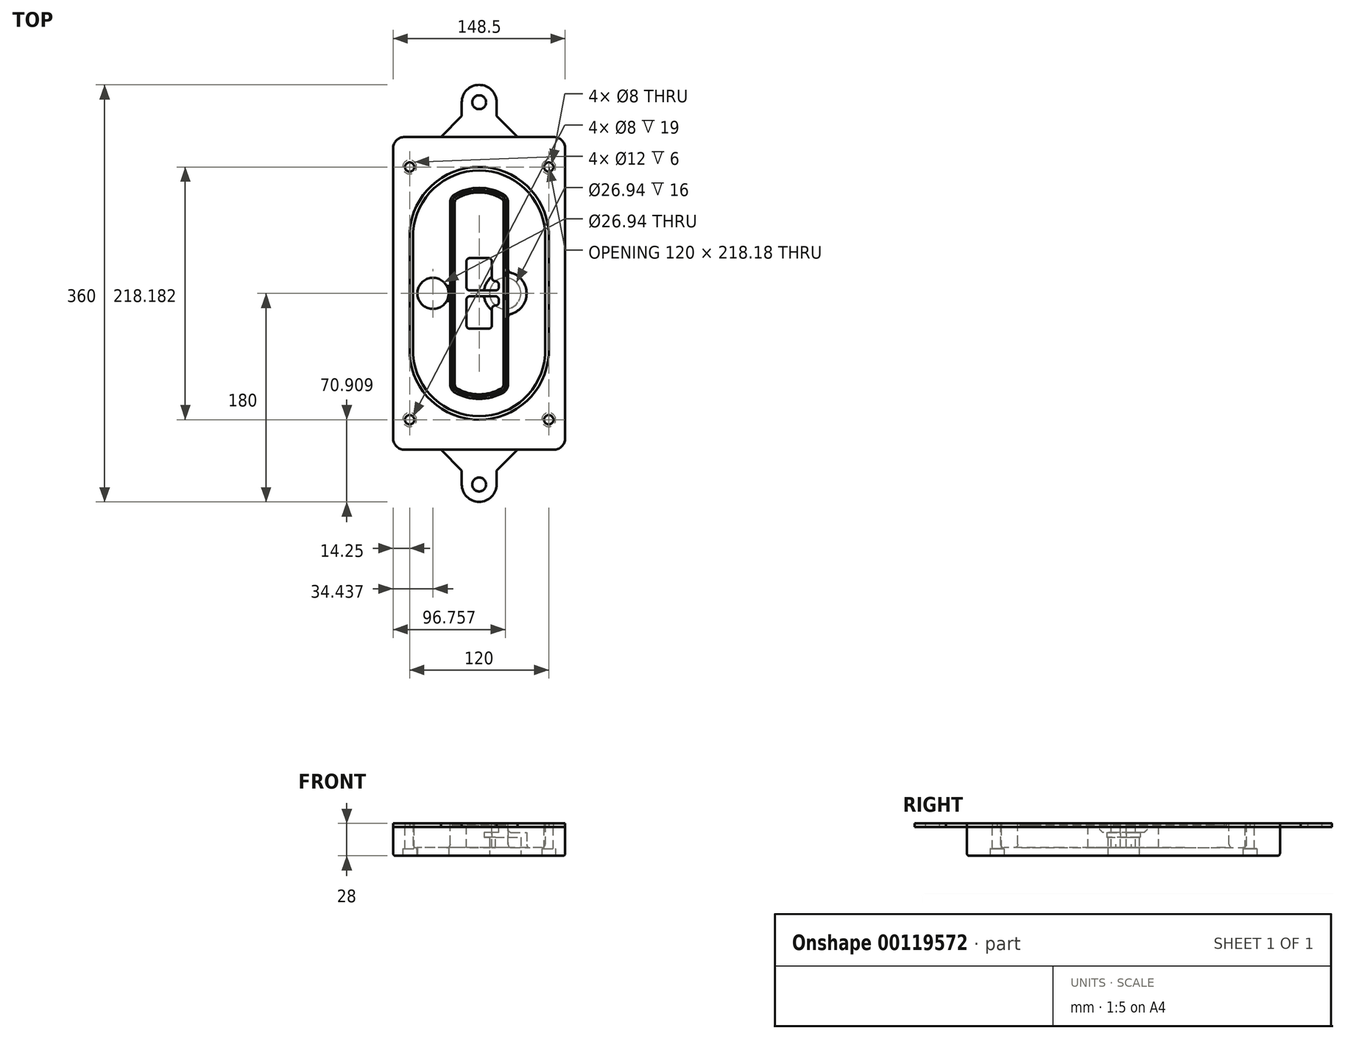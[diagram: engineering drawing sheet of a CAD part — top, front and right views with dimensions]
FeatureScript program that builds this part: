
annotation { "Feature Type Name" : "Feature", "Feature Type Description" : "" }
export const myFeature = defineFeature(function(context is Context, id is Id, definition is map)
    precondition{}
    {
        {
            var Q0;
            Q0=qCreatedBy(makeId("Top.planeOp"),FACE);
            var sketch = newSketch(context, id + "F0", { "sketchPlane" : qUnion([Q0])});
            skPoint(sketch, "E0.rect.middle", {"position": v(0, 0) * mm});
            skLineSegment(sketch, "E1.bottom", {"start": v(-64.25, -135) * mm, "end": v(64.25, -135) * mm});
            skLineSegment(sketch, "E1.top", {"start": v(-64.25, 135) * mm, "end": v(64.25, 135) * mm});
            skLineSegment(sketch, "E1.left", {"start": v(-74.25, -125) * mm, "end": v(-74.25, 125) * mm});
            skLineSegment(sketch, "E1.right", {"start": v(74.25, -125) * mm, "end": v(74.25, 125) * mm});
            skLineSegment(sketch, "E2", {"start": v(-74.25, 135) * mm, "end": v(74.25, -135) * mm, "construction": true});
            skLineSegment(sketch, "E3", {"start": v(74.25, 135) * mm, "end": v(-74.25, -135) * mm, "construction": true});
            skCircle(sketch, "E4", {"center": v(-60, 109.1) * mm, "radius": 4 * mm});
            skCircle(sketch, "E5", {"center": v(60, 109.1) * mm, "radius": 4 * mm});
            skCircle(sketch, "E6", {"center": v(60, -109.1) * mm, "radius": 4 * mm});
            skCircle(sketch, "E7", {"center": v(-60, -109.1) * mm, "radius": 4 * mm});
            skLineSegment(sketch, "E8", {"start": v(-60, 109.1) * mm, "end": v(60, 109.1) * mm, "construction": true});
            skLineSegment(sketch, "E9", {"start": v(60, 109.1) * mm, "end": v(60, -109.1) * mm, "construction": true});
            skLineSegment(sketch, "E10", {"start": v(60, -109.1) * mm, "end": v(-60, -109.1) * mm, "construction": true});
            skLineSegment(sketch, "E11", {"start": v(-60, -109.1) * mm, "end": v(-60, 109.1) * mm, "construction": true});
            skLineSegment(sketch, "E12", {"start": v(-60, 52.58) * mm, "end": v(-60, -52.58) * mm});
            skLineSegment(sketch, "E13", {"start": v(60, 52.58) * mm, "end": v(60, -52.58) * mm});
            skArc(sketch, "E14", {"start": v(59.97, 53.3) * mm, "mid": v(0, 109.1) * mm, "end": v(-59.97, 53.3) * mm});
            skArc(sketch, "E15", {"start": v(-59.97, -53.3) * mm, "mid": v(0, -109.1) * mm, "end": v(59.97, -53.3) * mm});
            skLineSegment(sketch, "E16", {"start": v(-60, 0) * mm, "end": v(60, 0) * mm, "construction": true});
            skPoint(sketch, "E17.visualSharp", {"position": v(-60, -45) * mm});
            skArc(sketch, "E17.filletArc", {"start": v(-60, -52.58) * mm, "mid": v(-60, -52.94) * mm, "end": v(-59.97, -53.3) * mm});
            skPoint(sketch, "E18.visualSharp", {"position": v(-60, 45) * mm});
            skArc(sketch, "E18.filletArc", {"start": v(-59.97, 53.3) * mm, "mid": v(-60, 52.94) * mm, "end": v(-60, 52.58) * mm});
            skPoint(sketch, "E19.visualSharp", {"position": v(60, 45) * mm});
            skArc(sketch, "E19.filletArc", {"start": v(60, 52.58) * mm, "mid": v(60, 52.94) * mm, "end": v(59.97, 53.3) * mm});
            skPoint(sketch, "E20.visualSharp", {"position": v(60, -45) * mm});
            skArc(sketch, "E20.filletArc", {"start": v(59.97, -53.3) * mm, "mid": v(60, -52.94) * mm, "end": v(60, -52.58) * mm});
            skPoint(sketch, "E21.visualSharp", {"position": v(-74.25, 135) * mm});
            skArc(sketch, "E21.filletArc", {"start": v(-64.25, 135) * mm, "mid": v(-71.32, 132.07) * mm, "end": v(-74.25, 125) * mm});
            skPoint(sketch, "E22.visualSharp", {"position": v(74.25, 135) * mm});
            skArc(sketch, "E22.filletArc", {"start": v(74.25, 125) * mm, "mid": v(71.32, 132.07) * mm, "end": v(64.25, 135) * mm});
            skPoint(sketch, "E23.visualSharp", {"position": v(74.25, -135) * mm});
            skArc(sketch, "E23.filletArc", {"start": v(64.25, -135) * mm, "mid": v(71.32, -132.07) * mm, "end": v(74.25, -125) * mm});
            skPoint(sketch, "E24.visualSharp", {"position": v(-74.25, -135) * mm});
            skArc(sketch, "E24.filletArc", {"start": v(-74.25, -125) * mm, "mid": v(-71.32, -132.07) * mm, "end": v(-64.25, -135) * mm});
            skArc(sketch, "E25.0", {"start": v(57, 52.58) * mm, "mid": v(57, 52.83) * mm, "end": v(56.98, 53.08) * mm});
            skLineSegment(sketch, "E25.1", {"start": v(57, 52.58) * mm, "end": v(57, -52.58) * mm});
            skArc(sketch, "E25.2", {"start": v(56.98, -53.08) * mm, "mid": v(57, -52.83) * mm, "end": v(57, -52.58) * mm});
            skArc(sketch, "E25.3", {"start": v(-56.98, -53.08) * mm, "mid": v(0, -106.1) * mm, "end": v(56.98, -53.08) * mm});
            skArc(sketch, "E25.4", {"start": v(-57, -52.58) * mm, "mid": v(-57, -52.83) * mm, "end": v(-56.98, -53.08) * mm});
            skArc(sketch, "E25.5", {"start": v(56.98, 53.08) * mm, "mid": v(0, 106.1) * mm, "end": v(-56.98, 53.08) * mm});
            skLineSegment(sketch, "E25.6", {"start": v(-57, 52.58) * mm, "end": v(-57, -52.58) * mm});
            skArc(sketch, "E25.7", {"start": v(-56.98, 53.08) * mm, "mid": v(-57, 52.83) * mm, "end": v(-57, 52.58) * mm});
            skArc(sketch, "E26.0", {"start": v(-63.96, 53.59) * mm, "mid": v(-64, 53.08) * mm, "end": v(-64, 52.58) * mm});
            skArc(sketch, "E26.1", {"start": v(63.96, 53.59) * mm, "mid": v(0, 113.1) * mm, "end": v(-63.96, 53.59) * mm});
            skArc(sketch, "E26.2", {"start": v(64, 52.58) * mm, "mid": v(64, 53.08) * mm, "end": v(63.96, 53.59) * mm});
            skLineSegment(sketch, "E26.3", {"start": v(64, 52.58) * mm, "end": v(64, -52.58) * mm});
            skArc(sketch, "E26.4", {"start": v(63.96, -53.59) * mm, "mid": v(64, -53.08) * mm, "end": v(64, -52.58) * mm});
            skLineSegment(sketch, "E26.5", {"start": v(-64, 52.58) * mm, "end": v(-64, -52.58) * mm});
            skArc(sketch, "E26.6", {"start": v(-63.96, -53.59) * mm, "mid": v(0, -113.1) * mm, "end": v(63.96, -53.59) * mm});
            skArc(sketch, "E26.7", {"start": v(-64, -52.58) * mm, "mid": v(-64, -53.08) * mm, "end": v(-63.96, -53.59) * mm});
            skSolve(sketch);
        }
        {
            var Q0;
            Q0=makeQuery(id+"F0.imprint","IMPRINT",FACE,{"disambiguationData":[TD([[makeQuery(id+"F0.imprint","IMPRINT",EDGE,{"derivedFrom":sQuery(id+"F0.wireOp",EDGE,"E1.bottom")}),1.0]])]});
            var Q1;
            Q1=makeQuery(id+"F0.imprint","IMPRINT",FACE,{"disambiguationData":[TD([[makeQuery(id+"F0.imprint","IMPRINT",EDGE,{"derivedFrom":sQuery(id+"F0.wireOp",EDGE,"E12")}),1.0]])]});
            var Q2;
            Q2=makeQuery(id+"F0.imprint","IMPRINT",FACE,{"disambiguationData":[TD([[makeQuery(id+"F0.imprint","IMPRINT",EDGE,{"derivedFrom":sQuery(id+"F0.wireOp",EDGE,"E25.0")}),1.0]])]});
            var Q3;
            Q3=makeQuery(id+"F0.imprint","IMPRINT",FACE,{"disambiguationData":[TD([[makeQuery(id+"F0.imprint","IMPRINT",EDGE,{"derivedFrom":sQuery(id+"F0.wireOp",EDGE,"E12")}),-1.0]])]});
            extrude(context, id + "F1", {"entities" : qUnion([Q0, Q1, Q2, Q3]), "oppositeDirection" : true, "depth" : 25 * mm});
        }
        {
            var Q0;
            Q0=makeQuery(id+"F0.imprint","IMPRINT",FACE,{"disambiguationData":[TD([[makeQuery(id+"F0.imprint","IMPRINT",EDGE,{"derivedFrom":sQuery(id+"F0.wireOp",EDGE,"E12")}),1.0]])]});
            extrude(context, id + "F2", {"entities" : qUnion([Q0]), "operationType" : NewBodyOperationType.ADD, "depth" : 3 * mm});
        }
        {
            var Q0;
            Q0=makeQuery(id+"F0.imprint","IMPRINT",FACE,{"disambiguationData":[TD([[makeQuery(id+"F0.imprint","IMPRINT",EDGE,{"derivedFrom":sQuery(id+"F0.wireOp",EDGE,"E25.0")}),1.0]])]});
            extrude(context, id + "F3", {"entities" : qUnion([Q0]), "operationType" : NewBodyOperationType.REMOVE, "oppositeDirection" : true, "depth" : 18 * mm});
        }
        {
            var Q0;
            Q0=makeQuery(id+"F2.opExtrude","CAP_FACE",FACE,{"disambiguationData":[OSD([sQuery(id+"F0.wireOp",EDGE,"E12"),sQuery(id+"F0.wireOp",EDGE,"E13"),sQuery(id+"F0.wireOp",EDGE,"E14"),sQuery(id+"F0.wireOp",EDGE,"E15"),sQuery(id+"F0.wireOp",EDGE,"E17.filletArc"),sQuery(id+"F0.wireOp",EDGE,"E18.filletArc"),sQuery(id+"F0.wireOp",EDGE,"E19.filletArc"),sQuery(id+"F0.wireOp",EDGE,"E20.filletArc"),sQuery(id+"F0.wireOp",EDGE,"E25.0"),sQuery(id+"F0.wireOp",EDGE,"E25.1"),sQuery(id+"F0.wireOp",EDGE,"E25.2"),sQuery(id+"F0.wireOp",EDGE,"E25.3"),sQuery(id+"F0.wireOp",EDGE,"E25.4"),sQuery(id+"F0.wireOp",EDGE,"E25.5"),sQuery(id+"F0.wireOp",EDGE,"E25.6"),sQuery(id+"F0.wireOp",EDGE,"E25.7")])],"isStart":false});
            var sketch = newSketch(context, id + "F4", { "sketchPlane" : qUnion([Q0])});
            skArc(sketch, "E27.0", {"start": v(-20.98, -85.5) * mm, "mid": v(0, -91.1) * mm, "end": v(20.98, -85.5) * mm});
            skArc(sketch, "E28.0", {"start": v(20.98, 85.5) * mm, "mid": v(0, 91.1) * mm, "end": v(-20.98, 85.5) * mm});
            skLineSegment(sketch, "E29", {"start": v(-25, 78.56) * mm, "end": v(-25, -78.56) * mm});
            skLineSegment(sketch, "E30", {"start": v(25, 78.56) * mm, "end": v(25, -78.56) * mm});
            skLineSegment(sketch, "E31", {"start": v(-25, 82.87) * mm, "end": v(25, 82.87) * mm, "construction": true});
            skLineSegment(sketch, "E32", {"start": v(-25, -82.87) * mm, "end": v(25, -82.87) * mm, "construction": true});
            skPoint(sketch, "E33.visualSharp", {"position": v(-25, 82.87) * mm});
            skArc(sketch, "E33.filletArc", {"start": v(-20.98, 85.5) * mm, "mid": v(-23.92, 82.56) * mm, "end": v(-25, 78.56) * mm});
            skPoint(sketch, "E34.visualSharp", {"position": v(25, 82.87) * mm});
            skArc(sketch, "E34.filletArc", {"start": v(25, 78.56) * mm, "mid": v(23.92, 82.56) * mm, "end": v(20.98, 85.5) * mm});
            skPoint(sketch, "E35.visualSharp", {"position": v(25, -82.87) * mm});
            skArc(sketch, "E35.filletArc", {"start": v(20.98, -85.5) * mm, "mid": v(23.92, -82.56) * mm, "end": v(25, -78.56) * mm});
            skPoint(sketch, "E36.visualSharp", {"position": v(-25, -82.87) * mm});
            skArc(sketch, "E36.filletArc", {"start": v(-25, -78.56) * mm, "mid": v(-23.92, -82.56) * mm, "end": v(-20.98, -85.5) * mm});
            skArc(sketch, "E37.0", {"start": v(56.98, 53.08) * mm, "mid": v(0, 106.1) * mm, "end": v(-56.98, 53.08) * mm});
            skArc(sketch, "E37.1", {"start": v(-56.98, 53.08) * mm, "mid": v(-57, 52.83) * mm, "end": v(-57, 52.58) * mm});
            skLineSegment(sketch, "E37.2", {"start": v(-57, 52.58) * mm, "end": v(-57, -52.58) * mm});
            skArc(sketch, "E37.3", {"start": v(-57, -52.58) * mm, "mid": v(-57, -52.83) * mm, "end": v(-56.98, -53.08) * mm});
            skArc(sketch, "E37.4", {"start": v(-56.98, -53.08) * mm, "mid": v(0, -106.1) * mm, "end": v(56.98, -53.08) * mm});
            skArc(sketch, "E37.5", {"start": v(56.98, -53.08) * mm, "mid": v(57, -52.83) * mm, "end": v(57, -52.58) * mm});
            skLineSegment(sketch, "E37.6", {"start": v(57, 52.58) * mm, "end": v(57, -52.58) * mm});
            skArc(sketch, "E37.7", {"start": v(57, 52.58) * mm, "mid": v(57, 52.83) * mm, "end": v(56.98, 53.08) * mm});
            skLineSegment(sketch, "E38.0", {"start": v(23, 78.56) * mm, "end": v(23, -78.56) * mm});
            skArc(sketch, "E38.1", {"start": v(19.99, -83.76) * mm, "mid": v(22.2, -81.56) * mm, "end": v(23, -78.56) * mm});
            skArc(sketch, "E38.2", {"start": v(-19.99, -83.76) * mm, "mid": v(0, -89.1) * mm, "end": v(19.99, -83.76) * mm});
            skArc(sketch, "E38.3", {"start": v(-23, -78.56) * mm, "mid": v(-22.2, -81.56) * mm, "end": v(-19.99, -83.76) * mm});
            skLineSegment(sketch, "E38.4", {"start": v(-23, 78.56) * mm, "end": v(-23, -78.56) * mm});
            skArc(sketch, "E38.5", {"start": v(23, 78.56) * mm, "mid": v(22.2, 81.56) * mm, "end": v(19.99, 83.76) * mm});
            skArc(sketch, "E38.6", {"start": v(-19.99, 83.76) * mm, "mid": v(-22.2, 81.56) * mm, "end": v(-23, 78.56) * mm});
            skArc(sketch, "E38.7", {"start": v(19.99, 83.76) * mm, "mid": v(0, 89.1) * mm, "end": v(-19.99, 83.76) * mm});
            skArc(sketch, "E39.0", {"start": v(21, 78.56) * mm, "mid": v(20.46, 80.56) * mm, "end": v(19, 82.02) * mm});
            skLineSegment(sketch, "E39.1", {"start": v(21, 78.56) * mm, "end": v(21, -78.56) * mm});
            skArc(sketch, "E39.2", {"start": v(19, -82.02) * mm, "mid": v(20.46, -80.56) * mm, "end": v(21, -78.56) * mm});
            skArc(sketch, "E39.3", {"start": v(-19, -82.02) * mm, "mid": v(0, -87.1) * mm, "end": v(19, -82.02) * mm});
            skArc(sketch, "E39.4", {"start": v(-21, -78.56) * mm, "mid": v(-20.46, -80.56) * mm, "end": v(-19, -82.02) * mm});
            skArc(sketch, "E39.5", {"start": v(19, 82.02) * mm, "mid": v(0, 87.1) * mm, "end": v(-19, 82.02) * mm});
            skLineSegment(sketch, "E39.6", {"start": v(-21, 78.56) * mm, "end": v(-21, -78.56) * mm});
            skArc(sketch, "E39.7", {"start": v(-19, 82.02) * mm, "mid": v(-20.46, 80.56) * mm, "end": v(-21, 78.56) * mm});
            skLineSegment(sketch, "E40", {"start": v(-25, 0) * mm, "end": v(25, 0) * mm, "construction": true});
            skLineSegment(sketch, "E41", {"start": v(-11, 5.5) * mm, "end": v(-11, 27.5) * mm});
            skLineSegment(sketch, "E42", {"start": v(-8, 30.5) * mm, "end": v(8, 30.5) * mm});
            skLineSegment(sketch, "E43", {"start": v(11, 27.5) * mm, "end": v(11, 13.5) * mm});
            skLineSegment(sketch, "E44", {"start": v(14, 10.5) * mm, "end": v(14, 10.5) * mm});
            skLineSegment(sketch, "E45", {"start": v(17, 7.5) * mm, "end": v(17, 5.5) * mm});
            skLineSegment(sketch, "E46", {"start": v(14, 2.5) * mm, "end": v(-8, 2.5) * mm});
            skPoint(sketch, "E47.visualSharp", {"position": v(-11, 30.5) * mm});
            skArc(sketch, "E47.filletArc", {"start": v(-8, 30.5) * mm, "mid": v(-10.12, 29.62) * mm, "end": v(-11, 27.5) * mm});
            skPoint(sketch, "E48.visualSharp", {"position": v(11, 30.5) * mm});
            skArc(sketch, "E48.filletArc", {"start": v(11, 27.5) * mm, "mid": v(10.12, 29.62) * mm, "end": v(8, 30.5) * mm});
            skPoint(sketch, "E49.visualSharp", {"position": v(11, 10.5) * mm});
            skArc(sketch, "E49.filletArc", {"start": v(11, 13.5) * mm, "mid": v(11.88, 11.38) * mm, "end": v(14, 10.5) * mm});
            skPoint(sketch, "E50.visualSharp", {"position": v(17, 10.5) * mm});
            skArc(sketch, "E50.filletArc", {"start": v(17, 7.5) * mm, "mid": v(16.12, 9.62) * mm, "end": v(14, 10.5) * mm});
            skPoint(sketch, "E51.visualSharp", {"position": v(17, 2.5) * mm});
            skArc(sketch, "E51.filletArc", {"start": v(14, 2.5) * mm, "mid": v(16.12, 3.38) * mm, "end": v(17, 5.5) * mm});
            skPoint(sketch, "E52.visualSharp", {"position": v(-11, 2.5) * mm});
            skArc(sketch, "E52.filletArc", {"start": v(-11, 5.5) * mm, "mid": v(-10.12, 3.38) * mm, "end": v(-8, 2.5) * mm});
            skLineSegment(sketch, "E53.0.MirrorCS", {"start": v(14, -2.5) * mm, "end": v(-8, -2.5) * mm});
            skArc(sketch, "E54.0.MirrorCS", {"start": v(-11, -5.5) * mm, "mid": v(-10.12, -3.38) * mm, "end": v(-8, -2.5) * mm});
            skLineSegment(sketch, "E55.0.MirrorCS", {"start": v(-11, -5.5) * mm, "end": v(-11, -27.5) * mm});
            skArc(sketch, "E56.0.MirrorCS", {"start": v(-8, -30.5) * mm, "mid": v(-10.12, -29.62) * mm, "end": v(-11, -27.5) * mm});
            skLineSegment(sketch, "E57.0.MirrorCS", {"start": v(-8, -30.5) * mm, "end": v(8, -30.5) * mm});
            skArc(sketch, "E58.0.MirrorCS", {"start": v(11, -27.5) * mm, "mid": v(10.12, -29.62) * mm, "end": v(8, -30.5) * mm});
            skLineSegment(sketch, "E59.0.MirrorCS", {"start": v(11, -27.5) * mm, "end": v(11, -13.5) * mm});
            skArc(sketch, "E60.0.MirrorCS", {"start": v(11, -13.5) * mm, "mid": v(11.88, -11.38) * mm, "end": v(14, -10.5) * mm});
            skArc(sketch, "E61.0.MirrorCS", {"start": v(17, -7.5) * mm, "mid": v(16.12, -9.62) * mm, "end": v(14, -10.5) * mm});
            skLineSegment(sketch, "E62.0.MirrorCS", {"start": v(17, -7.5) * mm, "end": v(17, -5.5) * mm});
            skArc(sketch, "E63.0.MirrorCS", {"start": v(14, -2.5) * mm, "mid": v(16.12, -3.38) * mm, "end": v(17, -5.5) * mm});
            skSolve(sketch);
        }
        {
            var Q0;
            Q0=makeQuery(id+"F4.imprint","IMPRINT",FACE,{"disambiguationData":[TD([[makeQuery(id+"F4.imprint","IMPRINT",EDGE,{"derivedFrom":sQuery(id+"F4.wireOp",EDGE,"E27.0")}),1.0]])]});
            var Q1;
            Q1=makeQuery(id+"F4.imprint","IMPRINT",FACE,{"disambiguationData":[TD([[makeQuery(id+"F4.imprint","IMPRINT",EDGE,{"derivedFrom":sQuery(id+"F4.wireOp",EDGE,"E38.0")}),-1.0]])]});
            var Q2;
            Q2=makeQuery(id+"F4.imprint","IMPRINT",FACE,{"disambiguationData":[TD([[makeQuery(id+"F4.imprint","IMPRINT",EDGE,{"derivedFrom":sQuery(id+"F4.wireOp",EDGE,"E39.0")}),1.0]])]});
            extrude(context, id + "F5", {"entities" : qUnion([Q0, Q1, Q2]), "operationType" : NewBodyOperationType.ADD, "endBound" : BoundingType.UP_TO_NEXT, "oppositeDirection" : true, "depth" : 25 * mm});
        }
        {
            var Q0;
            Q0=makeQuery(id+"F4.imprint","IMPRINT",FACE,{"disambiguationData":[TD([[makeQuery(id+"F4.imprint","IMPRINT",EDGE,{"derivedFrom":sQuery(id+"F4.wireOp",EDGE,"E38.0")}),-1.0]])]});
            extrude(context, id + "F6", {"entities" : qUnion([Q0]), "operationType" : NewBodyOperationType.REMOVE, "oppositeDirection" : true, "depth" : 2 * mm});
        }
        {
            var Q0;
            Q0=makeQuery(id+"F1.opExtrude","CAP_FACE",FACE,{"disambiguationData":[OSD([sQuery(id+"F0.wireOp",EDGE,"E1.bottom"),sQuery(id+"F0.wireOp",EDGE,"E1.top"),sQuery(id+"F0.wireOp",EDGE,"E1.left"),sQuery(id+"F0.wireOp",EDGE,"E1.right"),sQuery(id+"F0.wireOp",EDGE,"E4"),sQuery(id+"F0.wireOp",EDGE,"E5"),sQuery(id+"F0.wireOp",EDGE,"E6"),sQuery(id+"F0.wireOp",EDGE,"E7"),sQuery(id+"F0.wireOp",EDGE,"E21.filletArc"),sQuery(id+"F0.wireOp",EDGE,"E22.filletArc"),sQuery(id+"F0.wireOp",EDGE,"E23.filletArc"),sQuery(id+"F0.wireOp",EDGE,"E24.filletArc")])],"isStart":false});
            var sketch = newSketch(context, id + "F7", { "sketchPlane" : qUnion([Q0])});
            skCircle(sketch, "E64", {"center": v(22.5, 0) * mm, "radius": 13.47 * mm});
            skCircle(sketch, "E65", {"center": v(-39.81, 0) * mm, "radius": 13.47 * mm});
            skLineSegment(sketch, "E66", {"start": v(74.25, 0) * mm, "end": v(-74.25, 0) * mm});
            skCircle(sketch, "E67", {"center": v(22.5, 0) * mm, "radius": 18.47 * mm});
            skCircle(sketch, "E68", {"center": v(60, -109.1) * mm, "radius": 6 * mm});
            skCircle(sketch, "E69", {"center": v(-60, -109.1) * mm, "radius": 6 * mm});
            skCircle(sketch, "E70", {"center": v(-60, 109.1) * mm, "radius": 6 * mm});
            skCircle(sketch, "E71", {"center": v(60, 109.1) * mm, "radius": 6 * mm});
            skSolve(sketch);
        }
        {
            var Q0;
            {var subQ1=sQuery(id+"F7.wireOp",EDGE,"E66");var subQ4=sQuery(id+"F7.wireOp",EDGE,"E64");var subQ6=makeQuery(id+"F7.imprint","INTERSECT",VERTEX,{"disambiguationData":[OD(0.0)],"derivedFrom":[subQ4,subQ1]});Q0=makeQuery(id+"F7.imprint","IMPRINT",FACE,{"disambiguationData":[TD([[makeQuery(id+"F7.imprint","IMPRINT",EDGE,{"disambiguationData":[TD([[subQ6,-1.0]])],"derivedFrom":subQ4}),-1.0]])]});}
            var Q1;
            {var subQ0=sQuery(id+"F7.wireOp",EDGE,"E66");var subQ1=sQuery(id+"F7.wireOp",EDGE,"E64");var subQ3=makeQuery(id+"F7.imprint","INTERSECT",VERTEX,{"disambiguationData":[OD(0.0)],"derivedFrom":[subQ1,subQ0]});Q1=makeQuery(id+"F7.imprint","IMPRINT",FACE,{"disambiguationData":[TD([[makeQuery(id+"F7.imprint","IMPRINT",EDGE,{"disambiguationData":[TD([[subQ3,-1.0]])],"derivedFrom":subQ1}),1.0]])]});}
            var Q2;
            {var subQ0=sQuery(id+"F7.wireOp",EDGE,"E66");var subQ1=sQuery(id+"F7.wireOp",EDGE,"E64");var subQ3=makeQuery(id+"F7.imprint","INTERSECT",VERTEX,{"disambiguationData":[OD(0.0)],"derivedFrom":[subQ1,subQ0]});Q2=makeQuery(id+"F7.imprint","IMPRINT",FACE,{"disambiguationData":[TD([[makeQuery(id+"F7.imprint","IMPRINT",EDGE,{"disambiguationData":[TD([[subQ3,1.0]])],"derivedFrom":subQ1}),1.0]])]});}
            var Q3;
            {var subQ1=sQuery(id+"F7.wireOp",EDGE,"E66");var subQ4=sQuery(id+"F7.wireOp",EDGE,"E64");var subQ6=makeQuery(id+"F7.imprint","INTERSECT",VERTEX,{"disambiguationData":[OD(0.0)],"derivedFrom":[subQ4,subQ1]});Q3=makeQuery(id+"F7.imprint","IMPRINT",FACE,{"disambiguationData":[TD([[makeQuery(id+"F7.imprint","IMPRINT",EDGE,{"disambiguationData":[TD([[subQ6,1.0]])],"derivedFrom":subQ4}),-1.0]])]});}
            extrude(context, id + "F8", {"entities" : qUnion([Q0, Q1, Q2, Q3]), "operationType" : NewBodyOperationType.ADD, "oppositeDirection" : true, "depth" : 20 * mm});
        }
        {
            var Q0;
            {var subQ0=sQuery(id+"F7.wireOp",EDGE,"E66");var subQ1=sQuery(id+"F7.wireOp",EDGE,"E64");var subQ3=makeQuery(id+"F7.imprint","INTERSECT",VERTEX,{"disambiguationData":[OD(0.0)],"derivedFrom":[subQ1,subQ0]});Q0=makeQuery(id+"F7.imprint","IMPRINT",FACE,{"disambiguationData":[TD([[makeQuery(id+"F7.imprint","IMPRINT",EDGE,{"disambiguationData":[TD([[subQ3,-1.0]])],"derivedFrom":subQ1}),1.0]])]});}
            var Q1;
            {var subQ0=sQuery(id+"F7.wireOp",EDGE,"E66");var subQ1=sQuery(id+"F7.wireOp",EDGE,"E64");var subQ3=makeQuery(id+"F7.imprint","INTERSECT",VERTEX,{"disambiguationData":[OD(0.0)],"derivedFrom":[subQ1,subQ0]});Q1=makeQuery(id+"F7.imprint","IMPRINT",FACE,{"disambiguationData":[TD([[makeQuery(id+"F7.imprint","IMPRINT",EDGE,{"disambiguationData":[TD([[subQ3,1.0]])],"derivedFrom":subQ1}),1.0]])]});}
            extrude(context, id + "F9", {"entities" : qUnion([Q0, Q1]), "operationType" : NewBodyOperationType.REMOVE, "oppositeDirection" : true, "depth" : 16 * mm});
        }
        {
            var Q0;
            {var subQ0=sQuery(id+"F7.wireOp",EDGE,"E66");var subQ1=sQuery(id+"F7.wireOp",EDGE,"E65");var subQ3=makeQuery(id+"F7.imprint","INTERSECT",VERTEX,{"disambiguationData":[OD(0.0)],"derivedFrom":[subQ1,subQ0]});Q0=makeQuery(id+"F7.imprint","IMPRINT",FACE,{"disambiguationData":[TD([[makeQuery(id+"F7.imprint","IMPRINT",EDGE,{"disambiguationData":[TD([[subQ3,-1.0]])],"derivedFrom":subQ1}),1.0]])]});}
            var Q1;
            {var subQ0=sQuery(id+"F7.wireOp",EDGE,"E66");var subQ1=sQuery(id+"F7.wireOp",EDGE,"E65");var subQ3=makeQuery(id+"F7.imprint","INTERSECT",VERTEX,{"disambiguationData":[OD(0.0)],"derivedFrom":[subQ1,subQ0]});Q1=makeQuery(id+"F7.imprint","IMPRINT",FACE,{"disambiguationData":[TD([[makeQuery(id+"F7.imprint","IMPRINT",EDGE,{"disambiguationData":[TD([[subQ3,1.0]])],"derivedFrom":subQ1}),1.0]])]});}
            extrude(context, id + "F10", {"entities" : qUnion([Q0, Q1]), "operationType" : NewBodyOperationType.REMOVE, "oppositeDirection" : true, "depth" : 25 * mm});
        }
        {
            var Q0;
            Q0=makeQuery(id+"F7.imprint","IMPRINT",FACE,{"disambiguationData":[TD([[makeQuery(id+"F7.imprint","IMPRINT",EDGE,{"derivedFrom":sQuery(id+"F7.wireOp",EDGE,"E68")}),1.0]])]});
            var Q1;
            Q1=makeQuery(id+"F7.imprint","IMPRINT",FACE,{"disambiguationData":[TD([[makeQuery(id+"F7.imprint","IMPRINT",EDGE,{"derivedFrom":makeQuery(id+"F1.opExtrude","CAP_EDGE",EDGE,{"disambiguationData":[OSD([sQuery(id+"F0.wireOp",EDGE,"E5")])],"isStart":false})}),-1.0]])]});
            var Q2;
            Q2=makeQuery(id+"F7.imprint","IMPRINT",FACE,{"disambiguationData":[TD([[makeQuery(id+"F7.imprint","IMPRINT",EDGE,{"derivedFrom":sQuery(id+"F7.wireOp",EDGE,"E69")}),1.0]])]});
            var Q3;
            Q3=makeQuery(id+"F7.imprint","IMPRINT",FACE,{"disambiguationData":[TD([[makeQuery(id+"F7.imprint","IMPRINT",EDGE,{"derivedFrom":makeQuery(id+"F1.opExtrude","CAP_EDGE",EDGE,{"disambiguationData":[OSD([sQuery(id+"F0.wireOp",EDGE,"E4")])],"isStart":false})}),-1.0]])]});
            var Q4;
            Q4=makeQuery(id+"F7.imprint","IMPRINT",FACE,{"disambiguationData":[TD([[makeQuery(id+"F7.imprint","IMPRINT",EDGE,{"derivedFrom":sQuery(id+"F7.wireOp",EDGE,"E70")}),1.0]])]});
            var Q5;
            Q5=makeQuery(id+"F7.imprint","IMPRINT",FACE,{"disambiguationData":[TD([[makeQuery(id+"F7.imprint","IMPRINT",EDGE,{"derivedFrom":makeQuery(id+"F1.opExtrude","CAP_EDGE",EDGE,{"disambiguationData":[OSD([sQuery(id+"F0.wireOp",EDGE,"E7")])],"isStart":false})}),-1.0]])]});
            var Q6;
            Q6=makeQuery(id+"F7.imprint","IMPRINT",FACE,{"disambiguationData":[TD([[makeQuery(id+"F7.imprint","IMPRINT",EDGE,{"derivedFrom":sQuery(id+"F7.wireOp",EDGE,"E71")}),1.0]])]});
            var Q7;
            Q7=makeQuery(id+"F7.imprint","IMPRINT",FACE,{"disambiguationData":[TD([[makeQuery(id+"F7.imprint","IMPRINT",EDGE,{"derivedFrom":makeQuery(id+"F1.opExtrude","CAP_EDGE",EDGE,{"disambiguationData":[OSD([sQuery(id+"F0.wireOp",EDGE,"E6")])],"isStart":false})}),-1.0]])]});
            extrude(context, id + "F11", {"entities" : qUnion([Q0, Q1, Q2, Q3, Q4, Q5, Q6, Q7]), "operationType" : NewBodyOperationType.REMOVE, "oppositeDirection" : true, "depth" : 6 * mm});
        }
        {
            var Q0;
            Q0=makeQuery(id+"F9.boolean.opBoolean","COPY",FACE,{"derivedFrom":makeQuery(id+"F9.opExtrude","CAP_FACE",FACE,{"disambiguationData":[OSD([sQuery(id+"F7.wireOp",EDGE,"E64")])],"isStart":false})});
            var sketch = newSketch(context, id + "F12", { "sketchPlane" : qUnion([Q0])});
            skArc(sketch, "E72.0", {"start": v(11, 14.45) * mm, "mid": v(6.45, 9.13) * mm, "end": v(4.2, 2.5) * mm});
            skArc(sketch, "E72.1", {"start": v(4.2, -2.5) * mm, "mid": v(6.45, -9.13) * mm, "end": v(11, -14.45) * mm});
            skLineSegment(sketch, "E73", {"start": v(4.2, -2.5) * mm, "end": v(14, -2.5) * mm});
            skLineSegment(sketch, "E74.0", {"start": v(14, 2.5) * mm, "end": v(4.2, 2.5) * mm});
            skArc(sketch, "E74.1", {"start": v(14, 2.5) * mm, "mid": v(16.12, 3.38) * mm, "end": v(17, 5.5) * mm});
            skLineSegment(sketch, "E74.2", {"start": v(17, 7.5) * mm, "end": v(17, 5.5) * mm});
            skArc(sketch, "E74.3", {"start": v(17, 7.5) * mm, "mid": v(16.12, 9.62) * mm, "end": v(14, 10.5) * mm});
            skArc(sketch, "E74.4", {"start": v(11, 13.5) * mm, "mid": v(11.88, 11.38) * mm, "end": v(14, 10.5) * mm});
            skLineSegment(sketch, "E74.5", {"start": v(11, 14.45) * mm, "end": v(11, 13.5) * mm});
            skLineSegment(sketch, "E74.7", {"start": v(14, -2.5) * mm, "end": v(4.2, -2.5) * mm});
            skArc(sketch, "E74.8", {"start": v(14, -2.5) * mm, "mid": v(16.12, -3.38) * mm, "end": v(17, -5.5) * mm});
            skLineSegment(sketch, "E74.9", {"start": v(17, -7.5) * mm, "end": v(17, -5.5) * mm});
            skArc(sketch, "E74.10", {"start": v(17, -7.5) * mm, "mid": v(16.12, -9.62) * mm, "end": v(14, -10.5) * mm});
            skArc(sketch, "E74.11", {"start": v(11, -13.5) * mm, "mid": v(11.88, -11.38) * mm, "end": v(14, -10.5) * mm});
            skLineSegment(sketch, "E74.12", {"start": v(11, -14.45) * mm, "end": v(11, -13.5) * mm});
            skPoint(sketch, "E75.orphan", {"position": v(11, -27.5) * mm});
            skPoint(sketch, "E76.orphan", {"position": v(-8, -2.5) * mm});
            skPoint(sketch, "E77.orphan", {"position": v(-8, 2.5) * mm});
            skPoint(sketch, "E78.orphan", {"position": v(11, 27.5) * mm});
            skSolve(sketch);
        }
        {
            var Q0;
            {var subQ7=sQuery(id+"F12.wireOp",EDGE,"E72.0");var subQ14=sQuery(id+"F12.wireOp",EDGE,"E72.1");var subQ16=sQuery(id+"F12.wireOp",EDGE,"E74.1");var subQ18=sQuery(id+"F12.wireOp",EDGE,"E74.8");Q0=qUnion([makeQuery(id+"F12.imprint","IMPRINT",FACE,{"disambiguationData":[TD([[makeQuery(id+"F12.imprint","IMPRINT",EDGE,{"derivedFrom":subQ7}),1.0]])]}),makeQuery(id+"F12.imprint","IMPRINT",FACE,{"disambiguationData":[TD([[makeQuery(id+"F12.imprint","IMPRINT",EDGE,{"derivedFrom":subQ14}),1.0]])]}),makeQuery(id+"F12.imprint","IMPRINT",FACE,{"disambiguationData":[TD([[makeQuery(id+"F12.imprint","IMPRINT",EDGE,{"derivedFrom":subQ16}),1.0]])]}),makeQuery(id+"F12.imprint","IMPRINT",FACE,{"disambiguationData":[TD([[makeQuery(id+"F12.imprint","IMPRINT",EDGE,{"derivedFrom":subQ18}),-1.0]])]})]);}
            var Q1;
            Q1=makeQuery(id+"F5.boolean.opBoolean","SPLIT",FACE,{"disambiguationData":[TD([makeQuery(id+"F5.opExtrude","SWEPT_FACE",FACE,{"disambiguationData":[OSD([sQuery(id+"F4.wireOp",EDGE,"E41")])]})])],"derivedFrom":makeQuery(id+"F3.boolean.opBoolean","COPY",FACE,{"derivedFrom":makeQuery(id+"F3.opExtrude","CAP_FACE",FACE,{"disambiguationData":[OSD([sQuery(id+"F0.wireOp",EDGE,"E25.0"),sQuery(id+"F0.wireOp",EDGE,"E25.1"),sQuery(id+"F0.wireOp",EDGE,"E25.2"),sQuery(id+"F0.wireOp",EDGE,"E25.3"),sQuery(id+"F0.wireOp",EDGE,"E25.4"),sQuery(id+"F0.wireOp",EDGE,"E25.5"),sQuery(id+"F0.wireOp",EDGE,"E25.6"),sQuery(id+"F0.wireOp",EDGE,"E25.7")])],"isStart":false})})});
            extrude(context, id + "F13", {"entities" : qUnion([Q0]), "operationType" : NewBodyOperationType.REMOVE, "endBound" : BoundingType.UP_TO_SURFACE, "endBoundEntityFace" : qUnion([Q1]), "depth" : 25 * mm});
        }
        {
            var Q0;
            Q0=makeQuery(id+"F3.boolean.opBoolean","COPY",EDGE,{"derivedFrom":makeQuery(id+"F3.opExtrude","CAP_EDGE",EDGE,{"disambiguationData":[OSD([sQuery(id+"F0.wireOp",EDGE,"E25.6")])],"isStart":false})});
            var Q1;
            Q1=makeQuery(id+"F8.boolean.opBoolean","INTERSECT",EDGE,{"derivedFrom":[makeQuery(id+"F5.opExtrude","SWEPT_FACE",FACE,{"disambiguationData":[OSD([sQuery(id+"F4.wireOp",EDGE,"E30")])]}),makeQuery(id+"F8.opExtrude","CAP_FACE",FACE,{"disambiguationData":[OSD([sQuery(id+"F7.wireOp",EDGE,"E67")])],"isStart":false})]});
            var Q2;
            Q2=makeQuery(id+"F8.boolean.opBoolean","INTERSECT",EDGE,{"disambiguationData":[OD(1.0)],"derivedFrom":[makeQuery(id+"F5.opExtrude","SWEPT_FACE",FACE,{"disambiguationData":[OSD([sQuery(id+"F4.wireOp",EDGE,"E30")])]}),makeQuery(id+"F8.opExtrude","SWEPT_FACE",FACE,{"disambiguationData":[OSD([sQuery(id+"F7.wireOp",EDGE,"E67")])]})]});
            var Q3;
            {var subQ0=sQuery(id+"F4.wireOp",EDGE,"E30");Q3=makeQuery(id+"F8.boolean.opBoolean","SPLIT",EDGE,{"disambiguationData":[TD([makeQuery(id+"F5.opExtrude","SWEPT_FACE",FACE,{"disambiguationData":[OSD([sQuery(id+"F4.wireOp",EDGE,"E35.filletArc")])]})])],"derivedFrom":makeQuery(id+"F5.opExtrude","CAP_EDGE",EDGE,{"disambiguationData":[OSD([subQ0])],"isStart":false})});}
            var Q4;
            {var subQ0=sQuery(id+"F0.wireOp",EDGE,"E25.7");var subQ1=sQuery(id+"F0.wireOp",EDGE,"E25.1");var subQ2=sQuery(id+"F0.wireOp",EDGE,"E25.6");var subQ3=sQuery(id+"F0.wireOp",EDGE,"E25.5");var subQ4=sQuery(id+"F0.wireOp",EDGE,"E25.4");var subQ5=sQuery(id+"F0.wireOp",EDGE,"E25.0");var subQ6=sQuery(id+"F0.wireOp",EDGE,"E25.2");var subQ7=sQuery(id+"F0.wireOp",EDGE,"E25.3");Q4=makeQuery(id+"F8.boolean.opBoolean","INTERSECT",EDGE,{"derivedFrom":[makeQuery(id+"F5.boolean.opBoolean","SPLIT",FACE,{"disambiguationData":[TD([makeQuery(id+"F2.opExtrude","SWEPT_FACE",FACE,{"disambiguationData":[OSD([subQ5])]})])],"derivedFrom":makeQuery(id+"F3.boolean.opBoolean","COPY",FACE,{"derivedFrom":makeQuery(id+"F3.opExtrude","CAP_FACE",FACE,{"disambiguationData":[OSD([subQ5,subQ1,subQ6,subQ7,subQ4,subQ3,subQ2,subQ0])],"isStart":false})})}),makeQuery(id+"F8.opExtrude","SWEPT_FACE",FACE,{"disambiguationData":[OSD([sQuery(id+"F7.wireOp",EDGE,"E67")])]})]});}
            var Q5;
            Q5=makeQuery(id+"F8.boolean.opBoolean","INTERSECT",EDGE,{"disambiguationData":[OD(0.0)],"derivedFrom":[makeQuery(id+"F5.opExtrude","SWEPT_FACE",FACE,{"disambiguationData":[OSD([sQuery(id+"F4.wireOp",EDGE,"E30")])]}),makeQuery(id+"F8.opExtrude","SWEPT_FACE",FACE,{"disambiguationData":[OSD([sQuery(id+"F7.wireOp",EDGE,"E67")])]})]});
            fillet(context, id + "F14", {"entities" : qUnion([Q0, Q1, Q2, Q3, Q4, Q5]), "radius" : 3 * mm, "tangentPropagation" : true, "allowEdgeOverflow" : false});
        }
        {
            var Q0;
            Q0=makeQuery(id+"F1.opExtrude","CAP_EDGE",EDGE,{"disambiguationData":[OSD([sQuery(id+"F0.wireOp",EDGE,"E1.bottom")])],"isStart":false});
            fillet(context, id + "F15", {"entities" : qUnion([Q0]), "radius" : 2 * mm, "tangentPropagation" : true, "allowEdgeOverflow" : false});
        }
        {
            var Q0;
            Q0=makeQuery(id+"F0.imprint","IMPRINT",FACE,{"disambiguationData":[TD([[makeQuery(id+"F0.imprint","IMPRINT",EDGE,{"derivedFrom":sQuery(id+"F0.wireOp",EDGE,"E1.bottom")}),1.0]])]});
            var sketch = newSketch(context, id + "F16", { "sketchPlane" : qUnion([Q0])});
            skLineSegment(sketch, "E79", {"start": v(0, 135) * mm, "end": v(0, 165) * mm, "construction": true});
            skPoint(sketch, "E79.endSnap0", {"position": v(0, 135) * mm});
            skCircle(sketch, "E80", {"center": v(0, 165) * mm, "radius": 6 * mm});
            skArc(sketch, "E81", {"start": v(-15, 165) * mm, "mid": v(0, 180) * mm, "end": v(15, 165) * mm});
            skLineSegment(sketch, "E82", {"start": v(-15, 165) * mm, "end": v(-15, 153) * mm});
            skLineSegment(sketch, "E83", {"start": v(-15, 153) * mm, "end": v(-33, 135) * mm});
            skLineSegment(sketch, "E84", {"start": v(15, 165) * mm, "end": v(15, 153) * mm});
            skLineSegment(sketch, "E85", {"start": v(-33, 135) * mm, "end": v(0, 135) * mm, "construction": true});
            skLineSegment(sketch, "E86", {"start": v(15, 153) * mm, "end": v(33, 135) * mm});
            skLineSegment(sketch, "E87", {"start": v(33, 135) * mm, "end": v(0, 135) * mm, "construction": true});
            skLineSegment(sketch, "E88.MirrorCS", {"start": v(-15, -165) * mm, "end": v(-15, -153) * mm});
            skLineSegment(sketch, "E89.MirrorCS", {"start": v(15, -165) * mm, "end": v(15, -153) * mm});
            skArc(sketch, "E90.MirrorCS", {"start": v(-15, -165) * mm, "mid": v(0, -180) * mm, "end": v(15, -165) * mm});
            skCircle(sketch, "E91.MirrorC", {"center": v(0, -165) * mm, "radius": 6 * mm});
            skPoint(sketch, "E92.MirrorP", {"position": v(0, -135) * mm});
            skLineSegment(sketch, "E93.MirrorCS", {"start": v(15, -153) * mm, "end": v(33, -135) * mm});
            skLineSegment(sketch, "E94.MirrorCS", {"start": v(33, -135) * mm, "end": v(0, -135) * mm});
            skLineSegment(sketch, "E95.MirrorCS", {"start": v(-15, -153) * mm, "end": v(-33, -135) * mm});
            skLineSegment(sketch, "E96.MirrorCS", {"start": v(0, -135) * mm, "end": v(0, -165) * mm, "construction": true});
            skLineSegment(sketch, "E97.MirrorCS", {"start": v(-33, -135) * mm, "end": v(0, -135) * mm});
            skLineSegment(sketch, "E98.0", {"start": v(-64.25, -135) * mm, "end": v(64.25, -135) * mm});
            skArc(sketch, "E99.0.0", {"start": v(-74.25, -125) * mm, "mid": v(-71.32, -132.07) * mm, "end": v(-64.25, -135) * mm});
            skArc(sketch, "E99.0.2", {"start": v(64.25, -135) * mm, "mid": v(71.32, -132.07) * mm, "end": v(74.25, -125) * mm});
            skLineSegment(sketch, "E99.0.3", {"start": v(74.25, -125) * mm, "end": v(74.25, 125) * mm});
            skArc(sketch, "E99.0.4", {"start": v(74.25, 125) * mm, "mid": v(71.32, 132.07) * mm, "end": v(64.25, 135) * mm});
            skLineSegment(sketch, "E99.0.5", {"start": v(64.25, 135) * mm, "end": v(-64.25, 135) * mm});
            skArc(sketch, "E99.0.6", {"start": v(-64.25, 135) * mm, "mid": v(-71.32, 132.07) * mm, "end": v(-74.25, 125) * mm});
            skLineSegment(sketch, "E99.0.7", {"start": v(-74.25, 125) * mm, "end": v(-74.25, -125) * mm});
            skSolve(sketch);
        }
        {
            var Q0;
            Q0=makeQuery(id+"F16.imprint","IMPRINT",FACE,{"disambiguationData":[TD([[makeQuery(id+"F16.imprint","IMPRINT",EDGE,{"derivedFrom":sQuery(id+"F16.wireOp",EDGE,"E89.MirrorCS")}),1.0]])]});
            var Q1;
            Q1=makeQuery(id+"F0.imprint","IMPRINT",FACE,{"disambiguationData":[TD([[makeQuery(id+"F0.imprint","IMPRINT",EDGE,{"derivedFrom":sQuery(id+"F0.wireOp",EDGE,"E1.bottom")}),1.0]])]});
            var Q2;
            Q2=makeQuery(id+"F0.imprint","IMPRINT",FACE,{"disambiguationData":[TD([[makeQuery(id+"F0.imprint","IMPRINT",EDGE,{"derivedFrom":sQuery(id+"F0.wireOp",EDGE,"E12")}),-1.0]])]});
            var Q3;
            Q3=makeQuery(id+"F16.imprint","IMPRINT",FACE,{"disambiguationData":[TD([[makeQuery(id+"F16.imprint","IMPRINT",EDGE,{"derivedFrom":sQuery(id+"F16.wireOp",EDGE,"E80")}),-1.0]])]});
            var Q4;
            Q4=makeQuery(id+"F2.opExtrude","CAP_FACE",FACE,{"disambiguationData":[OSD([sQuery(id+"F0.wireOp",EDGE,"E12"),sQuery(id+"F0.wireOp",EDGE,"E13"),sQuery(id+"F0.wireOp",EDGE,"E14"),sQuery(id+"F0.wireOp",EDGE,"E15"),sQuery(id+"F0.wireOp",EDGE,"E17.filletArc"),sQuery(id+"F0.wireOp",EDGE,"E18.filletArc"),sQuery(id+"F0.wireOp",EDGE,"E19.filletArc"),sQuery(id+"F0.wireOp",EDGE,"E20.filletArc"),sQuery(id+"F0.wireOp",EDGE,"E25.0"),sQuery(id+"F0.wireOp",EDGE,"E25.1"),sQuery(id+"F0.wireOp",EDGE,"E25.2"),sQuery(id+"F0.wireOp",EDGE,"E25.3"),sQuery(id+"F0.wireOp",EDGE,"E25.4"),sQuery(id+"F0.wireOp",EDGE,"E25.5"),sQuery(id+"F0.wireOp",EDGE,"E25.6"),sQuery(id+"F0.wireOp",EDGE,"E25.7")])],"isStart":false});
            extrude(context, id + "F17", {"entities" : qUnion([Q0, Q1, Q2, Q3]), "endBound" : BoundingType.UP_TO_SURFACE, "endBoundEntityFace" : qUnion([Q4]), "depth" : 25 * mm});
        }
    });
